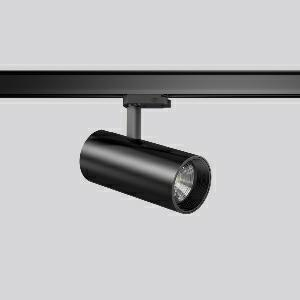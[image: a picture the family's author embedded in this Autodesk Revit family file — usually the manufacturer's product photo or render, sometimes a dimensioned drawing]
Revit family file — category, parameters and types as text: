
# Revit family: deecos_s_mini_742194_003_1_76_6529
name_source: partatom
category: Lighting Fixtures
units: mm (PartAtom-declared; Revit-internal decimal feet)

## family parameters
Cut with Voids When Loaded = No
Host = Face
Light Source = No
Part Type = Normal
Room Calculation Point = No
Round Connector Dimension = Use Diameter
Shared = No

## types (1)
- DEECOS S mini (1 x LED Modul 940, 2250 lm, 4000)
    Apparent Load = 22 VA
    Approval mark = CE
    CIE Flux Codes = 99 100 100 100 100
    Color Rendering = 92
    Color Temperature = 4000
    Default Elevation = 1800 mm
    Description = Series: DEECOS S mini
LED surface-mounted projector in modern design with no visible cooling ribs. Housing: die-cast aluminium, powder-coated. Rotation range: 356°. Swivel range: 90°. Black plastic ring and recessed LED to prevent glare from the side. Optical assembly with lens made of plastic (polycarbonate) for the best homogeneous light distribution - can be changed without tools. Best colour rendering index Ra>90. Superspot version with small spot LED. With adapter for RZB 3-circuit DALI tracks. Suitable for Track on ceiling, Wall track. High quality converter without flickering and stroboscopic effect. The following accessories can be mounted without use of tools: interchangeable lenses, decorative glasses, honeycomb louvre, clear and frosted diffusers, white interchangeable plastic ring. 
Colour: deep black, matt (RAL 9005)
Diameter: 87 mm
Height: 214 mm
Lamp: LED
Socket: without socket
Colour temperature: 4000K
Colour rendering index (CRI): 92
System power: 22 W
Rated luminous flux: 2250 lm
Luminous efficiency: 102 lm/W
Control gear: Converter, dimmable, DALI
Protection class: I
Type of protection: IP 20
    Height = 214 mm
    Lamp = 1 x LED Modul 940
    Lamp Light Flux = 2250 lm
    Lamp count = 1
    Length = 87 mm
    Lifetime = 50000 h
    Luminous efficacy = 102 lm/W
    Manufacturer = RZB
    ModVariant = No
    Model = 742194.003.1.76
    Mounting Place = Ceiling
    Mounting Type = Rail mounted
    Number of Poles = 1
    OnlyDefault = Yes
    Power Factor = 1
    Product Name = DEECOS S mini
    Product group = Track mounted projectors
    ProductGroupID = 301
    Protection Class = Protection class I
    Protection Degree = IP 20
    RLX_Detail_Level = 1
    RLX_Emergency_Light_Flux = 0 lm
    RLX_Emergency_Type = 0
    RLX_Emergency_Type_DB = No
    RlxData = <blob elided: 38601 chars, md5=874320e9>
    Socket = socket
    Standby Power = 0 W
    System Light Flux = 2250 lm
    System Power = 22 W
    Type Comments = Product without accessories
    Type Image = 741930.003.jpg
    URL = http://relux.com
    VarID = ---
    Voltage = 230 V
    Voltage Range = 220-240 V
    Weight = 0.00 kg
    Width = 0 mm  [stored 0 ft]

note: [stored X ft] marks values corroborated as IEEE doubles in the binary element streams (Revit-internal decimal feet)

## geometry (parser evidence)
native form markers: Blend x4, Sweep x12
no freeform markers — native parametric forms only
